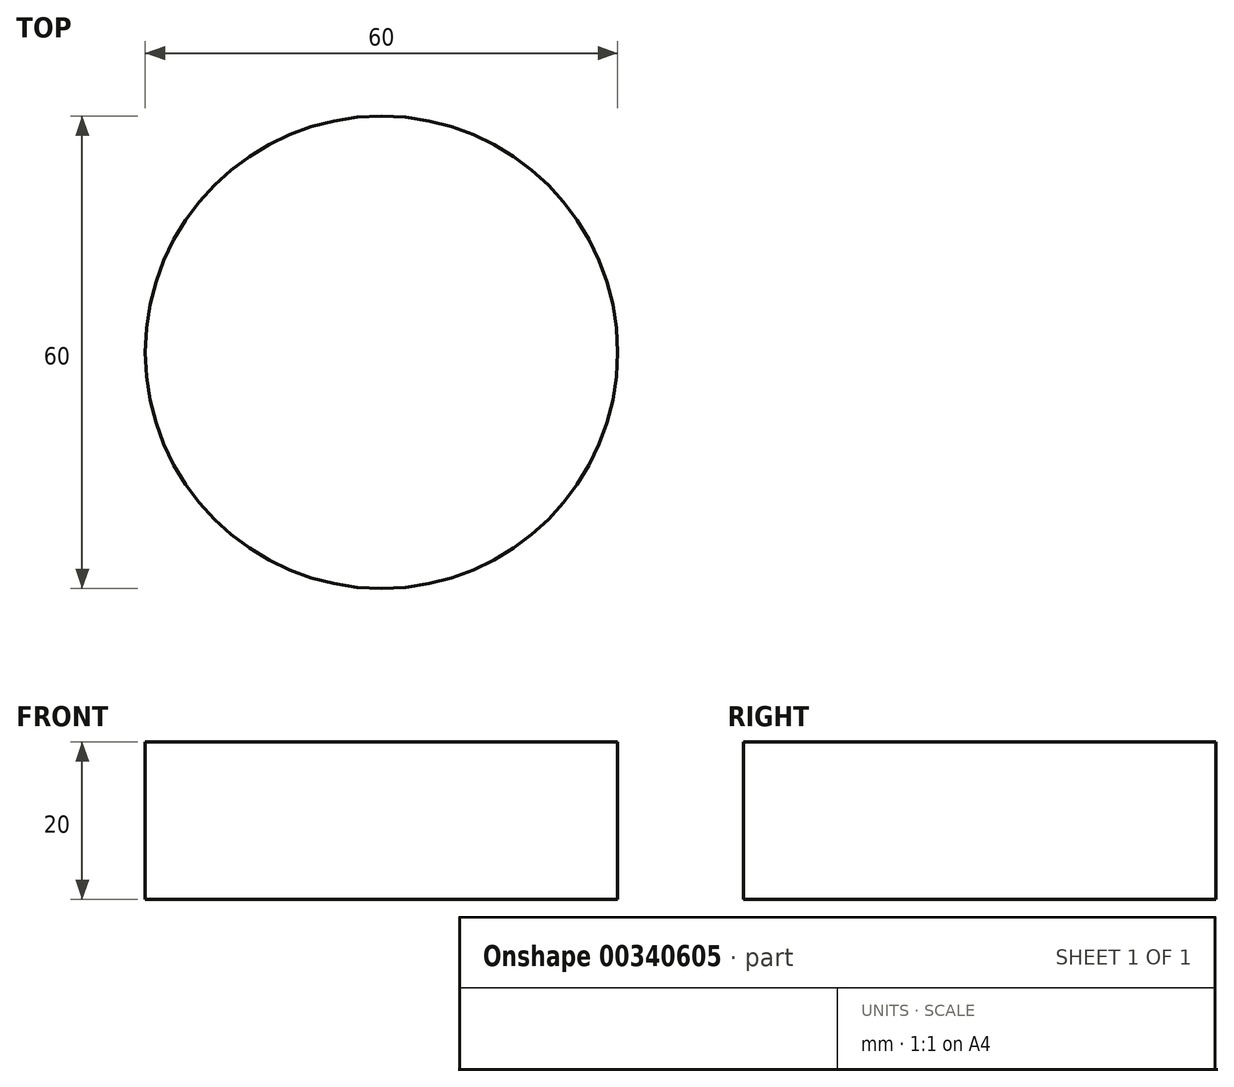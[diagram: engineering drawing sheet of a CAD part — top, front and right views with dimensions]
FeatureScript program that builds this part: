
annotation { "Feature Type Name" : "Feature", "Feature Type Description" : "" }
export const myFeature = defineFeature(function(context is Context, id is Id, definition is map)
    precondition{}
    {
        {
            var Q0;
            Q0=qCreatedBy(makeId("Top.planeOp"),FACE);
            var sketch = newSketch(context, id + "F0", { "sketchPlane" : qUnion([Q0])});
            skCircle(sketch, "E0", {"center": v(0, 0) * mm, "radius": 30 * mm});
            skSolve(sketch);
        }
        {
            var Q0;
            Q0=makeQuery(id+"F0.imprint","IMPRINT",FACE,{"disambiguationData":[TD([[makeQuery(id+"F0.imprint","IMPRINT",EDGE,{"derivedFrom":sQuery(id+"F0.wireOp",EDGE,"E0")}),1.0]])]});
            extrude(context, id + "F1", {"entities" : qUnion([Q0]), "depth" : 20 * mm});
        }
    });
